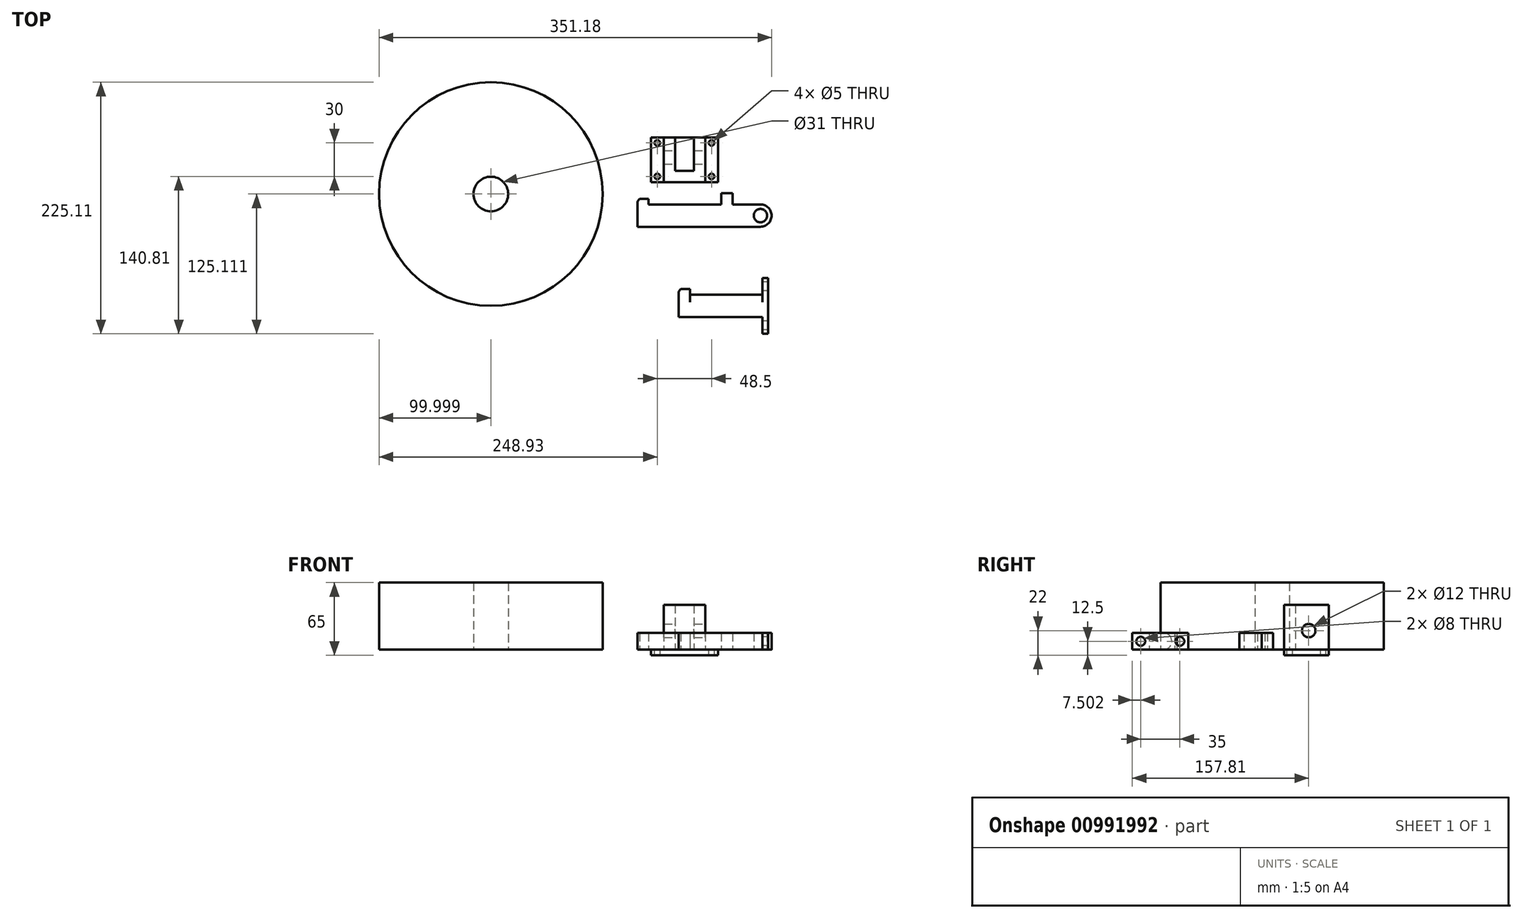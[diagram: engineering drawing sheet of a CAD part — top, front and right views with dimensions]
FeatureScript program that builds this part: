
annotation { "Feature Type Name" : "Feature", "Feature Type Description" : "" }
export const myFeature = defineFeature(function(context is Context, id is Id, definition is map)
    precondition{}
    {
        {
            var Q0;
            Q0=qCreatedBy(makeId("Top.planeOp"),FACE);
            var sketch = newSketch(context, id + "F0", { "sketchPlane" : qUnion([Q0])});
            skLineSegment(sketch, "E0.bottom", {"start": v(-32, 0) * mm, "end": v(33, 0) * mm});
            skLineSegment(sketch, "E0.top", {"start": v(-42, -20) * mm, "end": v(78, -20) * mm});
            skLineSegment(sketch, "E0.left", {"start": v(-42, 0) * mm, "end": v(-42, -20) * mm});
            skLineSegment(sketch, "E0.right", {"start": v(78, 0) * mm, "end": v(78, -20) * mm});
            skLineSegment(sketch, "E1.top", {"start": v(33, 10) * mm, "end": v(43, 10) * mm});
            skLineSegment(sketch, "E1.left", {"start": v(33, 0) * mm, "end": v(33, 10) * mm});
            skLineSegment(sketch, "E1.right", {"start": v(43, 0) * mm, "end": v(43, 10) * mm});
            skLineSegment(sketch, "E2.top", {"start": v(-40.03, 5) * mm, "end": v(-32, 5) * mm});
            skLineSegment(sketch, "E2.left", {"start": v(-42, 0) * mm, "end": v(-42, 2.88) * mm});
            skLineSegment(sketch, "E2.right", {"start": v(-32, 0) * mm, "end": v(-32, 5) * mm});
            skLineSegment(sketch, "E3", {"start": v(-42, 2.88) * mm, "end": v(-40.03, 5) * mm});
            skPoint(sketch, "E4", {"position": v(78, -10) * mm});
            skLineSegment(sketch, "E5.trimOffspring", {"start": v(43, 0) * mm, "end": v(78, 0) * mm});
            skLineSegment(sketch, "E6.bottom", {"start": v(30, 60) * mm, "end": v(18.5, 60) * mm});
            skLineSegment(sketch, "E6.top", {"start": v(30, 20) * mm, "end": v(-30, 20) * mm});
            skLineSegment(sketch, "E6.left", {"start": v(30, 60) * mm, "end": v(30, 20) * mm});
            skLineSegment(sketch, "E6.right", {"start": v(-30, 60) * mm, "end": v(-30, 20) * mm});
            skPoint(sketch, "E6.middle", {"position": v(0, 40) * mm});
            skLineSegment(sketch, "E7", {"start": v(-8.5, 60) * mm, "end": v(-8.5, 20) * mm});
            skLineSegment(sketch, "E8", {"start": v(8.5, 60) * mm, "end": v(8.5, 20) * mm});
            skPoint(sketch, "E9", {"position": v(0, 60) * mm});
            skLineSegment(sketch, "E10", {"start": v(8.5, 40) * mm, "end": v(-8.5, 40) * mm, "construction": true});
            skLineSegment(sketch, "E11", {"start": v(-18.5, 60) * mm, "end": v(-18.5, 20) * mm});
            skLineSegment(sketch, "E12", {"start": v(18.5, 60) * mm, "end": v(18.5, 20) * mm});
            skLineSegment(sketch, "E13", {"start": v(-18.5, 60) * mm, "end": v(-30, 60) * mm});
            skLineSegment(sketch, "E14", {"start": v(18.5, 60) * mm, "end": v(-18.5, 60) * mm});
            skPoint(sketch, "E15", {"position": v(-24.25, 60) * mm});
            skPoint(sketch, "E16", {"position": v(24.25, 60) * mm});
            skCircle(sketch, "E17", {"center": v(-24.25, 55) * mm, "radius": 2.5 * mm});
            skLineSegment(sketch, "E18", {"start": v(0, 60) * mm, "end": v(0, 20) * mm, "construction": true});
            skCircle(sketch, "E19.MirrorC", {"center": v(24.25, 55) * mm, "radius": 2.5 * mm});
            skCircle(sketch, "E20.MirrorC", {"center": v(24.25, 25) * mm, "radius": 2.5 * mm});
            skCircle(sketch, "E21.MirrorC", {"center": v(-24.25, 25) * mm, "radius": 2.5 * mm});
            skCircle(sketch, "E22", {"center": v(68, -10) * mm, "radius": 6 * mm});
            skLineSegment(sketch, "E23", {"start": v(-8.5, 30) * mm, "end": v(8.5, 30) * mm});
            skCircle(sketch, "E24", {"center": v(-14.3, -39.48) * mm, "radius": 5 * mm});
            skCircle(sketch, "E25", {"center": v(-173.18, 9.3) * mm, "radius": 100 * mm});
            skCircle(sketch, "E26", {"center": v(-173.18, 9.3) * mm, "radius": 15.5 * mm});
            skLineSegment(sketch, "E27.bottom", {"start": v(4.9, -80.8) * mm, "end": v(59.9, -80.8) * mm});
            skLineSegment(sketch, "E27.top", {"start": v(-5.1, -100.8) * mm, "end": v(74.9, -100.8) * mm});
            skLineSegment(sketch, "E27.left", {"start": v(-5.1, -80.8) * mm, "end": v(-5.1, -100.8) * mm});
            skLineSegment(sketch, "E27.right", {"start": v(74.9, -80.8) * mm, "end": v(74.9, -100.8) * mm});
            skLineSegment(sketch, "E28.right", {"start": v(69.9, -80.8) * mm, "end": v(69.9, -70.8) * mm});
            skLineSegment(sketch, "E29.top", {"start": v(-3.12, -75.8) * mm, "end": v(4.9, -75.8) * mm});
            skLineSegment(sketch, "E29.left", {"start": v(-5.1, -80.8) * mm, "end": v(-5.1, -77.93) * mm});
            skLineSegment(sketch, "E29.right", {"start": v(4.9, -80.8) * mm, "end": v(4.9, -75.8) * mm});
            skLineSegment(sketch, "E30", {"start": v(-5.1, -77.93) * mm, "end": v(-3.12, -75.8) * mm});
            skPoint(sketch, "E31", {"position": v(74.9, -90.8) * mm});
            skLineSegment(sketch, "E32.trimOffspring", {"start": v(69.9, -80.8) * mm, "end": v(74.9, -80.8) * mm});
            skLineSegment(sketch, "E33.bottom", {"start": v(74.9, -115.8) * mm, "end": v(69.9, -115.8) * mm});
            skLineSegment(sketch, "E33.top", {"start": v(74.9, -65.8) * mm, "end": v(69.9, -65.8) * mm});
            skLineSegment(sketch, "E33.left", {"start": v(74.9, -115.8) * mm, "end": v(74.9, -65.8) * mm});
            skLineSegment(sketch, "E33.right", {"start": v(69.9, -115.8) * mm, "end": v(69.9, -65.8) * mm});
            skLineSegment(sketch, "E34", {"start": v(59.9, -80.8) * mm, "end": v(69.9, -80.8) * mm});
            skSolve(sketch);
        }
        {
            var Q0;
            Q0=makeQuery(id+"F0.imprint","IMPRINT",FACE,{"disambiguationData":[TD([[makeQuery(id+"F0.imprint","IMPRINT",EDGE,{"derivedFrom":sQuery(id+"F0.wireOp",EDGE,"E0.bottom")}),-1.0]])]});
            extrude(context, id + "F1", {"entities" : qUnion([Q0]), "depth" : 15 * mm, "offsetDistance" : 25 * mm});
        }
        {
            var Q0;
            {var subQ1=sQuery(id+"F0.wireOp",EDGE,"E6.right");Q0=makeQuery(id+"F0.imprint","IMPRINT",FACE,{"disambiguationData":[TD([[makeQuery(id+"F0.imprint","IMPRINT",EDGE,{"derivedFrom":subQ1}),1.0]])]});}
            var Q1;
            {var subQ0=sQuery(id+"F0.wireOp",EDGE,"E11");Q1=makeQuery(id+"F0.imprint","IMPRINT",FACE,{"disambiguationData":[TD([[makeQuery(id+"F0.imprint","IMPRINT",EDGE,{"derivedFrom":subQ0}),1.0]])]});}
            var Q2;
            {var subQ5=sQuery(id+"F0.wireOp",EDGE,"E23");Q2=makeQuery(id+"F0.imprint","IMPRINT",FACE,{"disambiguationData":[TD([[makeQuery(id+"F0.imprint","IMPRINT",EDGE,{"derivedFrom":subQ5}),-1.0]])]});}
            var Q3;
            {var subQ0=sQuery(id+"F0.wireOp",EDGE,"E12");Q3=makeQuery(id+"F0.imprint","IMPRINT",FACE,{"disambiguationData":[TD([[makeQuery(id+"F0.imprint","IMPRINT",EDGE,{"derivedFrom":subQ0}),-1.0]])]});}
            var Q4;
            Q4=makeQuery(id+"F0.imprint","IMPRINT",FACE,{"disambiguationData":[TD([[makeQuery(id+"F0.imprint","IMPRINT",EDGE,{"derivedFrom":sQuery(id+"F0.wireOp",EDGE,"E6.bottom")}),1.0]])]});
            var Q5;
            {var subQ3=sQuery(id+"F0.wireOp",EDGE,"E23");Q5=makeQuery(id+"F0.imprint","IMPRINT",FACE,{"disambiguationData":[TD([[makeQuery(id+"F0.imprint","IMPRINT",EDGE,{"derivedFrom":subQ3}),1.0]])]});}
            extrude(context, id + "F2", {"entities" : qUnion([Q0, Q1, Q2, Q3, Q4, Q5]), "oppositeDirection" : true, "depth" : 5 * mm, "offsetDistance" : 25 * mm});
        }
        {
            var Q0;
            {var subQ0=sQuery(id+"F0.wireOp",EDGE,"E11");Q0=makeQuery(id+"F0.imprint","IMPRINT",FACE,{"disambiguationData":[TD([[makeQuery(id+"F0.imprint","IMPRINT",EDGE,{"derivedFrom":subQ0}),1.0]])]});}
            var Q1;
            {var subQ0=sQuery(id+"F0.wireOp",EDGE,"E12");Q1=makeQuery(id+"F0.imprint","IMPRINT",FACE,{"disambiguationData":[TD([[makeQuery(id+"F0.imprint","IMPRINT",EDGE,{"derivedFrom":subQ0}),-1.0]])]});}
            var Q2;
            {var subQ5=sQuery(id+"F0.wireOp",EDGE,"E23");Q2=makeQuery(id+"F0.imprint","IMPRINT",FACE,{"disambiguationData":[TD([[makeQuery(id+"F0.imprint","IMPRINT",EDGE,{"derivedFrom":subQ5}),-1.0]])]});}
            extrude(context, id + "F3", {"entities" : qUnion([Q0, Q1, Q2]), "operationType" : NewBodyOperationType.ADD, "depth" : 40 * mm, "offsetDistance" : 25 * mm});
        }
        {
            var Q0;
            Q0=makeQuery(id+"F1.opExtrude","SWEPT_EDGE",EDGE,{"disambiguationData":[OSD([sQuery(id+"F0.wireOp",EDGE,"E0.right"),sQuery(id+"F0.wireOp",EDGE,"E5.trimOffspring")])]});
            var Q1;
            Q1=makeQuery(id+"F1.opExtrude","SWEPT_EDGE",EDGE,{"disambiguationData":[OSD([sQuery(id+"F0.wireOp",EDGE,"E0.top"),sQuery(id+"F0.wireOp",EDGE,"E0.right")])]});
            fillet(context, id + "F4", {"entities" : qUnion([Q0, Q1]), "radius" : 10 * mm, "tangentPropagation" : true, "allowEdgeOverflow" : false});
        }
        {
            var Q0;
            Q0=makeQuery(id+"F3.opExtrude","SWEPT_FACE",FACE,{"disambiguationData":[OSD([sQuery(id+"F0.wireOp",EDGE,"E12")])]});
            var sketch = newSketch(context, id + "F5", { "sketchPlane" : qUnion([Q0])});
            skPoint(sketch, "E35.0", {"position": v(30, 40) * mm});
            skLineSegment(sketch, "E36", {"start": v(30, 40) * mm, "end": v(30, 0) * mm, "construction": true});
            skCircle(sketch, "E37", {"center": v(42, 17) * mm, "radius": 6 * mm});
            skLineSegment(sketch, "E38.0", {"start": v(60, 40) * mm, "end": v(30, 40) * mm});
            skLineSegment(sketch, "E39", {"start": v(30, 40) * mm, "end": v(20, 40) * mm});
            skPoint(sketch, "E40", {"position": v(45, 40) * mm});
            skSolve(sketch);
        }
        {
            var Q0;
            Q0=makeQuery(id+"F5.imprint","IMPRINT",FACE,{"disambiguationData":[TD([[makeQuery(id+"F5.imprint","IMPRINT",EDGE,{"derivedFrom":sQuery(id+"F5.wireOp",EDGE,"E37")}),1.0]])]});
            extrude(context, id + "F6", {"entities" : qUnion([Q0]), "operationType" : NewBodyOperationType.REMOVE, "oppositeDirection" : true, "depth" : 52.2 * mm, "offsetDistance" : 25 * mm});
        }
        {
            var Q0;
            Q0=makeQuery(id+"F0.imprint","IMPRINT",FACE,{"disambiguationData":[TD([[makeQuery(id+"F0.imprint","IMPRINT",EDGE,{"derivedFrom":sQuery(id+"F0.wireOp",EDGE,"E25")}),1.0]])]});
            extrude(context, id + "F7", {"entities" : qUnion([Q0]), "depth" : 60 * mm, "offsetDistance" : 25 * mm});
        }
        {
            var Q0;
            Q0=makeQuery(id+"F0.imprint","IMPRINT",FACE,{"disambiguationData":[TD([[makeQuery(id+"F0.imprint","IMPRINT",EDGE,{"derivedFrom":sQuery(id+"F0.wireOp",EDGE,"E27.bottom")}),-1.0]])]});
            var Q1;
            {var subQ5=sQuery(id+"F0.wireOp",EDGE,"E33.top");Q1=makeQuery(id+"F0.imprint","IMPRINT",FACE,{"disambiguationData":[TD([[makeQuery(id+"F0.imprint","IMPRINT",EDGE,{"derivedFrom":subQ5}),1.0]])]});}
            var Q2;
            {var subQ5=sQuery(id+"F0.wireOp",EDGE,"E33.bottom");Q2=makeQuery(id+"F0.imprint","IMPRINT",FACE,{"disambiguationData":[TD([[makeQuery(id+"F0.imprint","IMPRINT",EDGE,{"derivedFrom":subQ5}),-1.0]])]});}
            var Q3;
            {var subQ0=sQuery(id+"F0.wireOp",EDGE,"E33.left");var subQ1=sQuery(id+"F0.wireOp",EDGE,"E27.top");var subQ2=makeQuery(id+"F0.imprint","INTERSECT",VERTEX,{"derivedFrom":[subQ1,subQ0]});Q3=makeQuery(id+"F0.imprint","IMPRINT",FACE,{"disambiguationData":[TD([[makeQuery(id+"F0.imprint","IMPRINT",EDGE,{"disambiguationData":[TD([[subQ2,1.0]])],"derivedFrom":subQ1}),1.0]])]});}
            extrude(context, id + "F8", {"entities" : qUnion([Q0, Q1, Q2, Q3]), "depth" : 15 * mm, "offsetDistance" : 25 * mm});
        }
        {
            var Q0;
            {var subQ0=sQuery(id+"F0.wireOp",EDGE,"E33.right");Q0=makeQuery(id+"F8.opExtrude","SWEPT_FACE",FACE,{"disambiguationData":[OSD([subQ0]),TDD([makeQuery(id+"F0.imprint","IMPRINT",EDGE,{"disambiguationData":[TD([[makeQuery(id+"F0.imprint","INTERSECT",VERTEX,{"derivedFrom":[sQuery(id+"F0.wireOp",EDGE,"E33.bottom"),subQ0]}),-1.0]])],"derivedFrom":subQ0})])]});}
            var sketch = newSketch(context, id + "F9", { "sketchPlane" : qUnion([Q0])});
            skCircle(sketch, "E41", {"center": v(108.3, 7.5) * mm, "radius": 4 * mm});
            skPoint(sketch, "E41.centerSnap0", {"position": v(108.3, 15) * mm});
            skPoint(sketch, "E41.centerSnap1", {"position": v(115.8, 7.5) * mm});
            skLineSegment(sketch, "E42.0.0", {"start": v(65.8, 0) * mm, "end": v(80.8, 0) * mm});
            skLineSegment(sketch, "E42.0.1", {"start": v(80.8, 0) * mm, "end": v(80.8, 15) * mm});
            skLineSegment(sketch, "E42.0.2", {"start": v(80.8, 15) * mm, "end": v(65.8, 15) * mm});
            skLineSegment(sketch, "E42.0.3", {"start": v(65.8, 15) * mm, "end": v(65.8, 0) * mm});
            skCircle(sketch, "E43", {"center": v(73.3, 7.5) * mm, "radius": 4 * mm});
            skPoint(sketch, "E43.centerSnap0", {"position": v(65.8, 7.5) * mm});
            skPoint(sketch, "E43.centerSnap1", {"position": v(73.3, 15) * mm});
            skSolve(sketch);
        }
        {
            var Q0;
            Q0=makeQuery(id+"F9.imprint","IMPRINT",FACE,{"disambiguationData":[TD([[makeQuery(id+"F9.imprint","IMPRINT",EDGE,{"derivedFrom":sQuery(id+"F9.wireOp",EDGE,"E43")}),1.0]])]});
            var Q1;
            Q1=makeQuery(id+"F9.imprint","IMPRINT",FACE,{"disambiguationData":[TD([[makeQuery(id+"F9.imprint","IMPRINT",EDGE,{"derivedFrom":sQuery(id+"F9.wireOp",EDGE,"E41")}),1.0]])]});
            extrude(context, id + "F10", {"entities" : qUnion([Q0, Q1]), "operationType" : NewBodyOperationType.REMOVE, "oppositeDirection" : true, "depth" : 25 * mm, "offsetDistance" : 25 * mm});
        }
        {
            var Q0;
            Q0=makeQuery(id+"F8.opExtrude","CAP_EDGE",EDGE,{"disambiguationData":[OSD([sQuery(id+"F0.wireOp",EDGE,"E27.bottom"),sQuery(id+"F0.wireOp",EDGE,"E34")])],"isStart":true});
            var Q1;
            Q1=makeQuery(id+"F8.opExtrude","CAP_EDGE",EDGE,{"disambiguationData":[OSD([sQuery(id+"F0.wireOp",EDGE,"E27.bottom"),sQuery(id+"F0.wireOp",EDGE,"E34")])],"isStart":false});
            fillet(context, id + "F11", {"entities" : qUnion([Q0, Q1]), "radius" : 6.76 * mm, "tangentPropagation" : true, "allowEdgeOverflow" : false});
        }
    });
